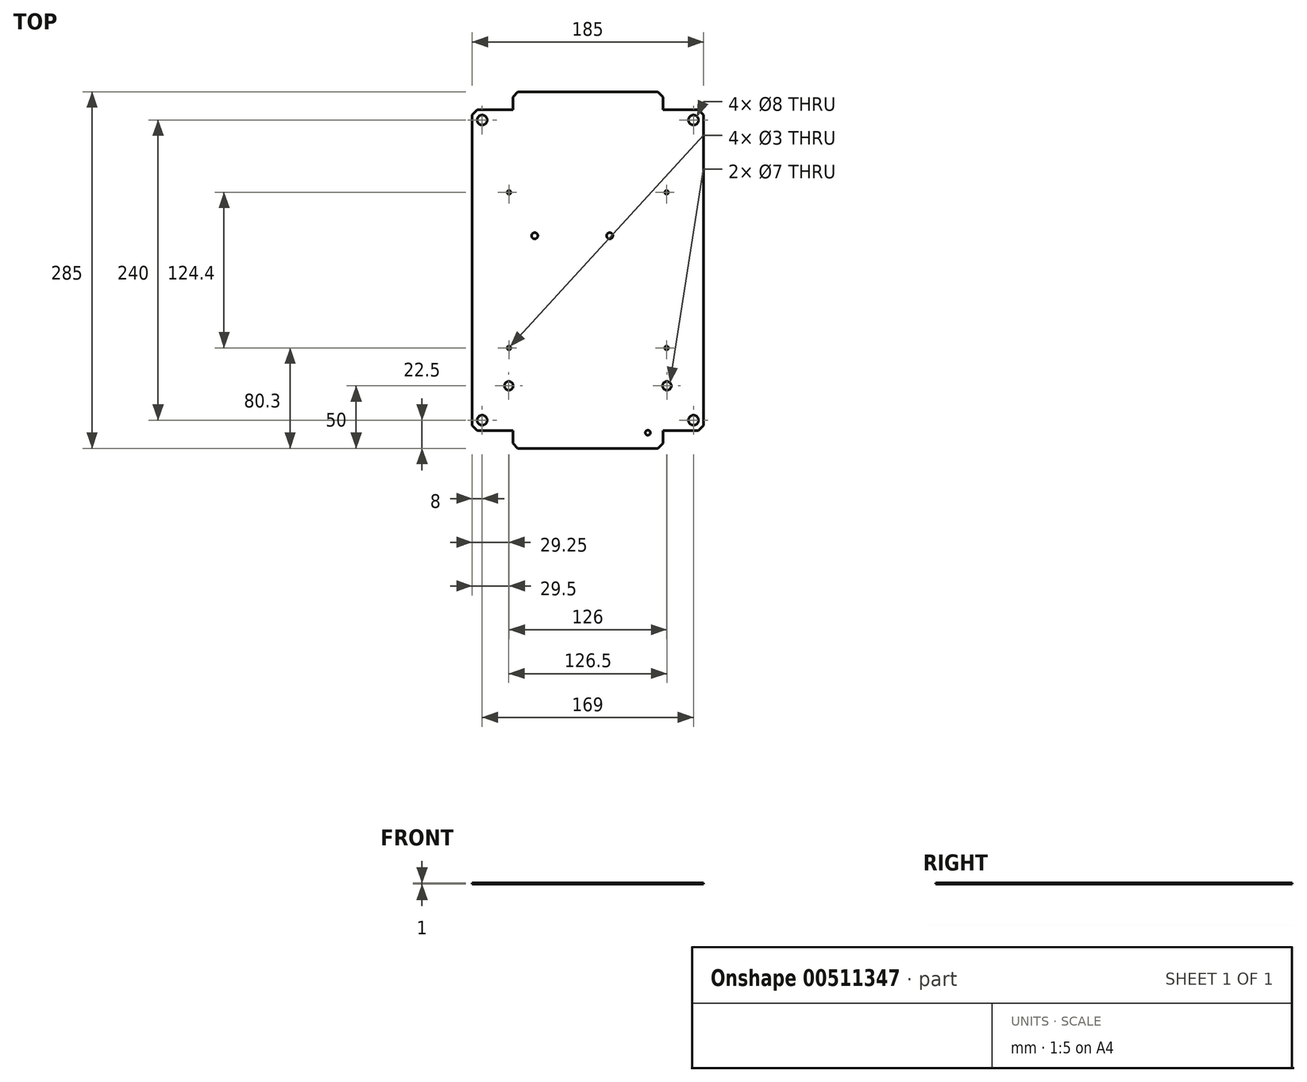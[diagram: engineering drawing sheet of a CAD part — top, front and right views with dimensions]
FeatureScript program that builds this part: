
annotation { "Feature Type Name" : "Feature", "Feature Type Description" : "" }
export const myFeature = defineFeature(function(context is Context, id is Id, definition is map)
    precondition{}
    {
        {
            var Q0;
            Q0=qCreatedBy(makeId("Top.planeOp"),FACE);
            var sketch = newSketch(context, id + "F0", { "sketchPlane" : qUnion([Q0])});
            skLineSegment(sketch, "E0", {"start": v(-92.5, 0) * mm, "end": v(-92.5, 128.2) * mm});
            skLineSegment(sketch, "E1", {"start": v(-92.5, 128.2) * mm, "end": v(-60, 128.2) * mm});
            skLineSegment(sketch, "E2", {"start": v(-60, 128.2) * mm, "end": v(-60, 142.5) * mm});
            skLineSegment(sketch, "E3", {"start": v(-60, 142.5) * mm, "end": v(0, 142.5) * mm});
            skCircle(sketch, "E4", {"center": v(-84.5, 120) * mm, "radius": 4 * mm});
            skCircle(sketch, "E5.MirrorC", {"center": v(84.5, 120) * mm, "radius": 4 * mm});
            skLineSegment(sketch, "E6.MirrorCS", {"start": v(60, 128.2) * mm, "end": v(60, 142.5) * mm});
            skLineSegment(sketch, "E7.MirrorCS", {"start": v(60, 142.5) * mm, "end": v(0, 142.5) * mm});
            skLineSegment(sketch, "E8.MirrorCS", {"start": v(92.5, 0) * mm, "end": v(92.5, 128.2) * mm});
            skLineSegment(sketch, "E9.MirrorCS", {"start": v(92.5, 128.2) * mm, "end": v(60, 128.2) * mm});
            skCircle(sketch, "E10.MirrorC", {"center": v(84.5, -120) * mm, "radius": 4 * mm});
            skCircle(sketch, "E11.MirrorC", {"center": v(-84.5, -120) * mm, "radius": 4 * mm});
            skLineSegment(sketch, "E12.MirrorCS", {"start": v(-60, -142.5) * mm, "end": v(0, -142.5) * mm});
            skLineSegment(sketch, "E13.MirrorCS", {"start": v(-60, -128.2) * mm, "end": v(-60, -142.5) * mm});
            skLineSegment(sketch, "E14.MirrorCS", {"start": v(-92.5, 0) * mm, "end": v(-92.5, -128.2) * mm});
            skLineSegment(sketch, "E15.MirrorCS", {"start": v(-92.5, -128.2) * mm, "end": v(-60, -128.2) * mm});
            skLineSegment(sketch, "E16.MirrorCS", {"start": v(60, -128.2) * mm, "end": v(60, -142.5) * mm});
            skLineSegment(sketch, "E17.MirrorCS", {"start": v(60, -142.5) * mm, "end": v(0, -142.5) * mm});
            skLineSegment(sketch, "E18.MirrorCS", {"start": v(92.5, -128.2) * mm, "end": v(60, -128.2) * mm});
            skLineSegment(sketch, "E19.MirrorCS", {"start": v(92.5, 0) * mm, "end": v(92.5, -128.2) * mm});
            skCircle(sketch, "E20", {"center": v(48, -130) * mm, "radius": 2 * mm});
            skCircle(sketch, "E21", {"center": v(-63, 62.2) * mm, "radius": 1.5 * mm});
            skCircle(sketch, "E22.MirrorC", {"center": v(63, 62.2) * mm, "radius": 1.5 * mm});
            skCircle(sketch, "E23.MirrorC", {"center": v(-63, -62.2) * mm, "radius": 1.5 * mm});
            skCircle(sketch, "E24.MirrorC", {"center": v(63, -62.2) * mm, "radius": 1.5 * mm});
            skCircle(sketch, "E25", {"center": v(-42.5, 27.5) * mm, "radius": 2.5 * mm});
            skCircle(sketch, "E26", {"center": v(17.5, 27.5) * mm, "radius": 2.5 * mm});
            skCircle(sketch, "E27", {"center": v(-63.25, -92.5) * mm, "radius": 3.5 * mm});
            skCircle(sketch, "E28.MirrorC", {"center": v(63.25, -92.5) * mm, "radius": 3.5 * mm});
            skSolve(sketch);
        }
        {
            var Q0;
            Q0=qSketchRegion(id+"F0",true);
            extrude(context, id + "F1", {"entities" : qUnion([Q0]), "endBound" : BoundingType.SYMMETRIC, "depth" : 1 * mm});
        }
        {
            var Q0;
            Q0=makeQuery(id+"F1.opExtrude","SWEPT_EDGE",EDGE,{"disambiguationData":[OSD([sQuery(id+"F0.wireOp",EDGE,"E0"),sQuery(id+"F0.wireOp",EDGE,"E1")])]});
            var Q1;
            Q1=makeQuery(id+"F1.opExtrude","SWEPT_EDGE",EDGE,{"disambiguationData":[OSD([sQuery(id+"F0.wireOp",EDGE,"E2"),sQuery(id+"F0.wireOp",EDGE,"E3")])]});
            var Q2;
            Q2=makeQuery(id+"F1.opExtrude","SWEPT_EDGE",EDGE,{"disambiguationData":[OSD([sQuery(id+"F0.wireOp",EDGE,"E6.MirrorCS"),sQuery(id+"F0.wireOp",EDGE,"E7.MirrorCS")])]});
            var Q3;
            Q3=makeQuery(id+"F1.opExtrude","SWEPT_EDGE",EDGE,{"disambiguationData":[OSD([sQuery(id+"F0.wireOp",EDGE,"E8.MirrorCS"),sQuery(id+"F0.wireOp",EDGE,"E9.MirrorCS")])]});
            var Q4;
            Q4=makeQuery(id+"F1.opExtrude","SWEPT_EDGE",EDGE,{"disambiguationData":[OSD([sQuery(id+"F0.wireOp",EDGE,"E18.MirrorCS"),sQuery(id+"F0.wireOp",EDGE,"E19.MirrorCS")])]});
            var Q5;
            Q5=makeQuery(id+"F1.opExtrude","SWEPT_EDGE",EDGE,{"disambiguationData":[OSD([sQuery(id+"F0.wireOp",EDGE,"E16.MirrorCS"),sQuery(id+"F0.wireOp",EDGE,"E17.MirrorCS")])]});
            var Q6;
            Q6=makeQuery(id+"F1.opExtrude","SWEPT_EDGE",EDGE,{"disambiguationData":[OSD([sQuery(id+"F0.wireOp",EDGE,"E12.MirrorCS"),sQuery(id+"F0.wireOp",EDGE,"E13.MirrorCS")])]});
            var Q7;
            Q7=makeQuery(id+"F1.opExtrude","SWEPT_EDGE",EDGE,{"disambiguationData":[OSD([sQuery(id+"F0.wireOp",EDGE,"E14.MirrorCS"),sQuery(id+"F0.wireOp",EDGE,"E15.MirrorCS")])]});
            chamfer(context, id + "F2", {"entities" : qUnion([Q0, Q1, Q2, Q3, Q4, Q5, Q6, Q7]), "width" : 4 * mm, "tangentPropagation" : true});
        }
    });
